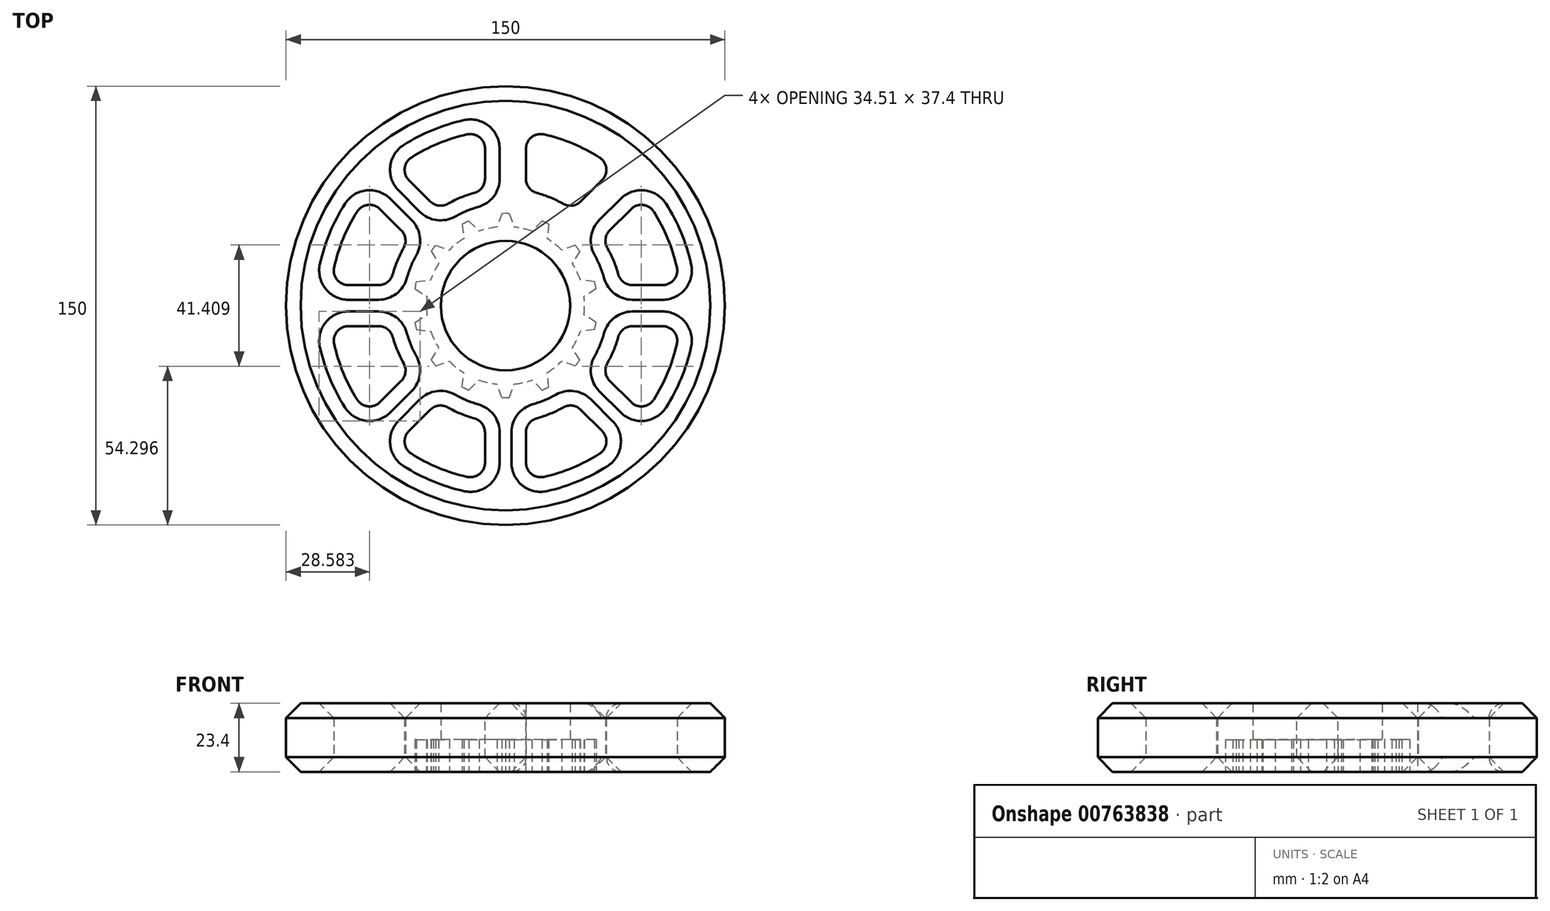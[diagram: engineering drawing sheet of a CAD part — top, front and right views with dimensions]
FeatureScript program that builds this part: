
annotation { "Feature Type Name" : "Feature", "Feature Type Description" : "" }
export const myFeature = defineFeature(function(context is Context, id is Id, definition is map)
    precondition{}
    {
        {
            var Q0;
            Q0=qCreatedBy(makeId("Top.planeOp"),FACE);
            var sketch = newSketch(context, id + "F0", { "sketchPlane" : qUnion([Q0])});
            skCircle(sketch, "E0", {"center": v(0, 0) * mm, "radius": 22.1 * mm});
            skCircle(sketch, "E1", {"center": v(0, 0) * mm, "radius": 75 * mm});
            skSolve(sketch);
        }
        {
            var Q0;
            Q0=qSketchRegion(id+"F0",true);
            extrude(context, id + "F1", {"entities" : qUnion([Q0]), "depth" : 23.4 * mm, "offsetDistance" : 25 * mm});
        }
        {
            var Q0;
            Q0=makeQuery(id+"F1.opExtrude","CAP_FACE",FACE,{"disambiguationData":[OSD([sQuery(id+"F0.wireOp",EDGE,"E0"),sQuery(id+"F0.wireOp",EDGE,"E1")])],"isStart":true});
            var sketch = newSketch(context, id + "F2", { "sketchPlane" : qUnion([Q0])});
            skCircle(sketch, "E2.0", {"center": v(0, 0) * mm, "radius": 22.1 * mm});
            skArc(sketch, "E3", {"start": v(2.9, -26.84) * mm, "mid": v(6, -26.32) * mm, "end": v(9.03, -25.44) * mm});
            skLineSegment(sketch, "E4", {"start": v(0, 0) * mm, "end": v(0, 59.3) * mm, "construction": true});
            skArc(sketch, "E5", {"start": v(0, -31.5) * mm, "mid": v(0.63, -31.5) * mm, "end": v(1.25, -31.48) * mm, "construction": true});
            skLineSegment(sketch, "E6", {"start": v(0, 31.5) * mm, "end": v(-1.25, 31.48) * mm});
            skLineSegment(sketch, "E7.MirrorCS", {"start": v(0, 31.5) * mm, "end": v(1.25, 31.48) * mm});
            skLineSegment(sketch, "E8", {"start": v(-1.25, 31.48) * mm, "end": v(-2.9, 26.84) * mm});
            skLineSegment(sketch, "E9", {"start": v(1.25, 31.48) * mm, "end": v(2.9, 26.84) * mm});
            skArc(sketch, "E10.1.0", {"start": v(0, -31.5) * mm, "mid": v(0.63, -31.5) * mm, "end": v(1.25, -31.48) * mm});
            skLineSegment(sketch, "E11.1.0", {"start": v(-12.53, 28.9) * mm, "end": v(-9.03, 25.44) * mm});
            skLineSegment(sketch, "E11.1.1", {"start": v(-14.78, 27.82) * mm, "end": v(-14.26, 22.93) * mm});
            skLineSegment(sketch, "E11.1.2", {"start": v(-13.67, 28.38) * mm, "end": v(-12.53, 28.9) * mm});
            skLineSegment(sketch, "E11.1.3", {"start": v(-13.67, 28.38) * mm, "end": v(-14.78, 27.82) * mm});
            skLineSegment(sketch, "E11.2.0", {"start": v(-23.83, 20.6) * mm, "end": v(-19.18, 19) * mm});
            skLineSegment(sketch, "E11.2.1", {"start": v(-25.39, 18.65) * mm, "end": v(-22.8, 14.47) * mm});
            skLineSegment(sketch, "E11.2.2", {"start": v(-24.63, 19.64) * mm, "end": v(-23.83, 20.6) * mm});
            skLineSegment(sketch, "E11.2.3", {"start": v(-24.63, 19.64) * mm, "end": v(-25.39, 18.65) * mm});
            skLineSegment(sketch, "E11.3.0", {"start": v(-30.4, 8.22) * mm, "end": v(-25.53, 8.8) * mm});
            skLineSegment(sketch, "E11.3.1", {"start": v(-30.96, 5.79) * mm, "end": v(-26.82, 3.15) * mm});
            skLineSegment(sketch, "E11.3.2", {"start": v(-30.71, 7) * mm, "end": v(-30.4, 8.22) * mm});
            skLineSegment(sketch, "E11.3.3", {"start": v(-30.71, 7) * mm, "end": v(-30.96, 5.79) * mm});
            skLineSegment(sketch, "E11.4.0", {"start": v(-30.96, -5.79) * mm, "end": v(-26.82, -3.15) * mm});
            skLineSegment(sketch, "E11.4.1", {"start": v(-30.4, -8.22) * mm, "end": v(-25.53, -8.8) * mm});
            skLineSegment(sketch, "E11.4.2", {"start": v(-30.71, -7) * mm, "end": v(-30.96, -5.79) * mm});
            skLineSegment(sketch, "E11.4.3", {"start": v(-30.71, -7) * mm, "end": v(-30.4, -8.22) * mm});
            skLineSegment(sketch, "E11.5.0", {"start": v(-25.39, -18.65) * mm, "end": v(-22.8, -14.47) * mm});
            skLineSegment(sketch, "E11.5.1", {"start": v(-23.83, -20.6) * mm, "end": v(-19.18, -19) * mm});
            skLineSegment(sketch, "E11.5.2", {"start": v(-24.63, -19.64) * mm, "end": v(-25.39, -18.65) * mm});
            skLineSegment(sketch, "E11.5.3", {"start": v(-24.63, -19.64) * mm, "end": v(-23.83, -20.6) * mm});
            skLineSegment(sketch, "E11.6.0", {"start": v(-14.78, -27.82) * mm, "end": v(-14.26, -22.93) * mm});
            skLineSegment(sketch, "E11.6.1", {"start": v(-12.53, -28.9) * mm, "end": v(-9.03, -25.44) * mm});
            skLineSegment(sketch, "E11.6.2", {"start": v(-13.67, -28.38) * mm, "end": v(-14.78, -27.82) * mm});
            skLineSegment(sketch, "E11.6.3", {"start": v(-13.67, -28.38) * mm, "end": v(-12.53, -28.9) * mm});
            skLineSegment(sketch, "E11.7.0", {"start": v(-1.25, -31.48) * mm, "end": v(-2.9, -26.84) * mm});
            skLineSegment(sketch, "E11.7.1", {"start": v(1.25, -31.48) * mm, "end": v(2.9, -26.84) * mm});
            skLineSegment(sketch, "E11.7.2", {"start": v(0, -31.5) * mm, "end": v(-1.25, -31.48) * mm});
            skLineSegment(sketch, "E11.7.3", {"start": v(0, -31.5) * mm, "end": v(1.25, -31.48) * mm});
            skLineSegment(sketch, "E11.8.0", {"start": v(12.53, -28.9) * mm, "end": v(9.03, -25.44) * mm});
            skLineSegment(sketch, "E11.8.1", {"start": v(14.78, -27.82) * mm, "end": v(14.26, -22.93) * mm});
            skLineSegment(sketch, "E11.8.2", {"start": v(13.67, -28.38) * mm, "end": v(12.53, -28.9) * mm});
            skLineSegment(sketch, "E11.8.3", {"start": v(13.67, -28.38) * mm, "end": v(14.78, -27.82) * mm});
            skLineSegment(sketch, "E11.9.0", {"start": v(23.83, -20.6) * mm, "end": v(19.18, -19) * mm});
            skLineSegment(sketch, "E11.9.1", {"start": v(25.39, -18.65) * mm, "end": v(22.8, -14.47) * mm});
            skLineSegment(sketch, "E11.9.2", {"start": v(24.63, -19.64) * mm, "end": v(23.83, -20.6) * mm});
            skLineSegment(sketch, "E11.9.3", {"start": v(24.63, -19.64) * mm, "end": v(25.39, -18.65) * mm});
            skLineSegment(sketch, "E11.10.0", {"start": v(30.4, -8.22) * mm, "end": v(25.53, -8.8) * mm});
            skLineSegment(sketch, "E11.10.1", {"start": v(30.96, -5.79) * mm, "end": v(26.82, -3.15) * mm});
            skLineSegment(sketch, "E11.10.2", {"start": v(30.71, -7) * mm, "end": v(30.4, -8.22) * mm});
            skLineSegment(sketch, "E11.10.3", {"start": v(30.71, -7) * mm, "end": v(30.96, -5.79) * mm});
            skLineSegment(sketch, "E11.11.0", {"start": v(30.96, 5.79) * mm, "end": v(26.82, 3.15) * mm});
            skLineSegment(sketch, "E11.11.1", {"start": v(30.4, 8.22) * mm, "end": v(25.53, 8.8) * mm});
            skLineSegment(sketch, "E11.11.2", {"start": v(30.71, 7) * mm, "end": v(30.96, 5.79) * mm});
            skLineSegment(sketch, "E11.11.3", {"start": v(30.71, 7) * mm, "end": v(30.4, 8.22) * mm});
            skLineSegment(sketch, "E11.12.0", {"start": v(25.39, 18.65) * mm, "end": v(22.8, 14.47) * mm});
            skLineSegment(sketch, "E11.12.1", {"start": v(23.83, 20.6) * mm, "end": v(19.18, 19) * mm});
            skLineSegment(sketch, "E11.12.2", {"start": v(24.63, 19.64) * mm, "end": v(25.39, 18.65) * mm});
            skLineSegment(sketch, "E11.12.3", {"start": v(24.63, 19.64) * mm, "end": v(23.83, 20.6) * mm});
            skLineSegment(sketch, "E11.13.0", {"start": v(14.78, 27.82) * mm, "end": v(14.26, 22.93) * mm});
            skLineSegment(sketch, "E11.13.1", {"start": v(12.53, 28.9) * mm, "end": v(9.03, 25.44) * mm});
            skLineSegment(sketch, "E11.13.2", {"start": v(13.67, 28.38) * mm, "end": v(14.78, 27.82) * mm});
            skLineSegment(sketch, "E11.13.3", {"start": v(13.67, 28.38) * mm, "end": v(12.53, 28.9) * mm});
            skArc(sketch, "E12.trimOffspring", {"start": v(-2.9, 26.84) * mm, "mid": v(-6, 26.32) * mm, "end": v(-9.03, 25.44) * mm, "construction": true});
            skPoint(sketch, "E13.start.orphan", {"position": v(0, 27) * mm});
            skArc(sketch, "E14.trimOffspring", {"start": v(-2.9, 26.84) * mm, "mid": v(-6, 26.32) * mm, "end": v(-9.03, 25.44) * mm});
            skArc(sketch, "E15.trimOffspring", {"start": v(-12.53, 28.9) * mm, "mid": v(-13.67, 28.38) * mm, "end": v(-14.78, 27.82) * mm, "construction": true});
            skArc(sketch, "E16.trimOffspring", {"start": v(-12.53, 28.9) * mm, "mid": v(-13.67, 28.38) * mm, "end": v(-14.78, 27.82) * mm});
            skArc(sketch, "E17.trimOffspring", {"start": v(1.25, 31.48) * mm, "mid": v(0, 31.5) * mm, "end": v(-1.25, 31.48) * mm, "construction": true});
            skArc(sketch, "E18.trimOffspring", {"start": v(1.25, 31.48) * mm, "mid": v(0, 31.5) * mm, "end": v(-1.25, 31.48) * mm});
            skArc(sketch, "E19.trimOffspring", {"start": v(9.03, 25.44) * mm, "mid": v(6, 26.32) * mm, "end": v(2.9, 26.84) * mm});
            skArc(sketch, "E20.trimOffspring", {"start": v(14.78, 27.82) * mm, "mid": v(13.67, 28.38) * mm, "end": v(12.53, 28.9) * mm, "construction": true});
            skArc(sketch, "E21.trimOffspring", {"start": v(14.78, 27.82) * mm, "mid": v(13.67, 28.38) * mm, "end": v(12.53, 28.9) * mm});
            skArc(sketch, "E22.trimOffspring", {"start": v(25.39, 18.65) * mm, "mid": v(24.63, 19.64) * mm, "end": v(23.83, 20.6) * mm, "construction": true});
            skArc(sketch, "E23.trimOffspring", {"start": v(19.18, 19) * mm, "mid": v(16.83, 21.1) * mm, "end": v(14.26, 22.93) * mm});
            skArc(sketch, "E24.trimOffspring", {"start": v(25.39, 18.65) * mm, "mid": v(24.63, 19.64) * mm, "end": v(23.83, 20.6) * mm});
            skArc(sketch, "E25.trimOffspring", {"start": v(25.53, 8.8) * mm, "mid": v(24.33, 11.71) * mm, "end": v(22.8, 14.47) * mm});
            skArc(sketch, "E26.trimOffspring", {"start": v(30.96, 5.79) * mm, "mid": v(30.71, 7) * mm, "end": v(30.4, 8.22) * mm, "construction": true});
            skArc(sketch, "E27.trimOffspring", {"start": v(30.96, 5.79) * mm, "mid": v(30.71, 7) * mm, "end": v(30.4, 8.22) * mm});
            skArc(sketch, "E28.trimOffspring", {"start": v(30.4, -8.22) * mm, "mid": v(30.71, -7) * mm, "end": v(30.96, -5.79) * mm, "construction": true});
            skArc(sketch, "E29.trimOffspring", {"start": v(30.4, -8.22) * mm, "mid": v(30.71, -7) * mm, "end": v(30.96, -5.79) * mm});
            skArc(sketch, "E30.trimOffspring", {"start": v(26.82, -3.15) * mm, "mid": v(27, 0) * mm, "end": v(26.82, 3.15) * mm});
            skArc(sketch, "E31.trimOffspring", {"start": v(22.8, -14.47) * mm, "mid": v(24.33, -11.71) * mm, "end": v(25.53, -8.8) * mm});
            skArc(sketch, "E32.trimOffspring", {"start": v(23.83, -20.6) * mm, "mid": v(24.63, -19.64) * mm, "end": v(25.39, -18.65) * mm, "construction": true});
            skArc(sketch, "E33.trimOffspring", {"start": v(23.83, -20.6) * mm, "mid": v(24.63, -19.64) * mm, "end": v(25.39, -18.65) * mm});
            skArc(sketch, "E34.trimOffspring", {"start": v(14.26, -22.93) * mm, "mid": v(16.83, -21.1) * mm, "end": v(19.18, -19) * mm});
            skArc(sketch, "E35.trimOffspring", {"start": v(12.53, -28.9) * mm, "mid": v(13.67, -28.38) * mm, "end": v(14.78, -27.82) * mm, "construction": true});
            skArc(sketch, "E36.trimOffspring", {"start": v(12.53, -28.9) * mm, "mid": v(13.67, -28.38) * mm, "end": v(14.78, -27.82) * mm});
            skPoint(sketch, "E37.orphan", {"position": v(0, -27) * mm});
            skArc(sketch, "E38.trimOffspring", {"start": v(-1.25, -31.48) * mm, "mid": v(-1.07, -31.48) * mm, "end": v(-0.88, -31.49) * mm, "construction": true});
            skArc(sketch, "E39.trimOffspring", {"start": v(-1.25, -31.48) * mm, "mid": v(-1.07, -31.48) * mm, "end": v(-0.88, -31.49) * mm});
            skArc(sketch, "E40.trimOffspring", {"start": v(-9.03, -25.44) * mm, "mid": v(-6, -26.32) * mm, "end": v(-2.9, -26.84) * mm, "construction": true});
            skArc(sketch, "E41.trimOffspring", {"start": v(-9.03, -25.44) * mm, "mid": v(-6, -26.32) * mm, "end": v(-2.9, -26.84) * mm});
            skArc(sketch, "E42.trimOffspring", {"start": v(-14.78, -27.82) * mm, "mid": v(-13.67, -28.38) * mm, "end": v(-12.53, -28.9) * mm, "construction": true});
            skArc(sketch, "E43.trimOffspring", {"start": v(-14.78, -27.82) * mm, "mid": v(-13.67, -28.38) * mm, "end": v(-12.53, -28.9) * mm});
            skArc(sketch, "E44.trimOffspring", {"start": v(-25.39, -18.65) * mm, "mid": v(-24.63, -19.64) * mm, "end": v(-23.83, -20.6) * mm, "construction": true});
            skArc(sketch, "E45.trimOffspring", {"start": v(-25.39, -18.65) * mm, "mid": v(-25.01, -19.15) * mm, "end": v(-24.63, -19.64) * mm});
            skArc(sketch, "E46.trimOffspring", {"start": v(-30.96, -5.79) * mm, "mid": v(-30.84, -6.4) * mm, "end": v(-30.71, -7) * mm, "construction": true});
            skArc(sketch, "E47.trimOffspring", {"start": v(-30.96, -5.79) * mm, "mid": v(-30.84, -6.4) * mm, "end": v(-30.71, -7) * mm});
            skArc(sketch, "E48.trimOffspring", {"start": v(-30.4, 8.22) * mm, "mid": v(-30.71, 7) * mm, "end": v(-30.96, 5.79) * mm, "construction": true});
            skArc(sketch, "E49.trimOffspring", {"start": v(-30.4, 8.22) * mm, "mid": v(-30.71, 7) * mm, "end": v(-30.96, 5.79) * mm});
            skArc(sketch, "E50.trimOffspring", {"start": v(-23.83, 20.6) * mm, "mid": v(-24.63, 19.64) * mm, "end": v(-25.39, 18.65) * mm, "construction": true});
            skArc(sketch, "E51.trimOffspring", {"start": v(-23.83, 20.6) * mm, "mid": v(-24.63, 19.64) * mm, "end": v(-25.39, 18.65) * mm});
            skArc(sketch, "E52.trimOffspring", {"start": v(-19.18, -19) * mm, "mid": v(-16.83, -21.1) * mm, "end": v(-14.26, -22.93) * mm});
            skArc(sketch, "E53.trimOffspring", {"start": v(-25.53, -8.8) * mm, "mid": v(-24.33, -11.71) * mm, "end": v(-22.8, -14.47) * mm});
            skArc(sketch, "E54.trimOffspring", {"start": v(-26.82, 3.15) * mm, "mid": v(-27, 0) * mm, "end": v(-26.82, -3.15) * mm});
            skArc(sketch, "E55.trimOffspring", {"start": v(-22.8, 14.47) * mm, "mid": v(-24.33, 11.71) * mm, "end": v(-25.53, 8.8) * mm, "construction": true});
            skArc(sketch, "E56.trimOffspring", {"start": v(-22.8, 14.47) * mm, "mid": v(-24.33, 11.71) * mm, "end": v(-25.53, 8.8) * mm});
            skArc(sketch, "E57.trimOffspring", {"start": v(-14.26, 22.93) * mm, "mid": v(-16.83, 21.1) * mm, "end": v(-19.18, 19) * mm, "construction": true});
            skArc(sketch, "E58.trimOffspring", {"start": v(-14.26, 22.93) * mm, "mid": v(-16.83, 21.1) * mm, "end": v(-19.18, 19) * mm});
            skSolve(sketch);
        }
        {
            var Q0;
            Q0=qSketchRegion(id+"F2",true);
            extrude(context, id + "F3", {"entities" : qUnion([Q0]), "operationType" : NewBodyOperationType.REMOVE, "oppositeDirection" : true, "depth" : 11 * mm, "offsetDistance" : 25 * mm});
        }
        {
            var Q0;
            Q0=makeQuery(id+"F1.opExtrude","CAP_FACE",FACE,{"disambiguationData":[OSD([sQuery(id+"F0.wireOp",EDGE,"E0"),sQuery(id+"F0.wireOp",EDGE,"E1")])],"isStart":true});
            var sketch = newSketch(context, id + "F4", { "sketchPlane" : qUnion([Q0])});
            skArc(sketch, "E59", {"start": v(-32.8, 22.9) * mm, "mid": v(-36.96, 15.3) * mm, "end": v(-39.38, 7) * mm});
            skArc(sketch, "E60", {"start": v(-47.09, 37.18) * mm, "mid": v(-55.43, 22.96) * mm, "end": v(-59.59, 7) * mm});
            skLineSegment(sketch, "E61", {"start": v(0, 0) * mm, "end": v(0, 117.13) * mm, "construction": true});
            skLineSegment(sketch, "E62", {"start": v(-7, 59.59) * mm, "end": v(-7, 39.38) * mm});
            skLineSegment(sketch, "E63.MirrorCS", {"start": v(7, 59.59) * mm, "end": v(7, 39.38) * mm});
            skLineSegment(sketch, "E64.1.0", {"start": v(-47.09, 37.18) * mm, "end": v(-32.8, 22.9) * mm});
            skLineSegment(sketch, "E64.1.1", {"start": v(-37.18, 47.09) * mm, "end": v(-22.9, 32.8) * mm});
            skLineSegment(sketch, "E64.2.0", {"start": v(-59.59, -7) * mm, "end": v(-39.38, -7) * mm});
            skLineSegment(sketch, "E64.2.1", {"start": v(-59.59, 7) * mm, "end": v(-39.38, 7) * mm});
            skLineSegment(sketch, "E64.3.0", {"start": v(-37.18, -47.09) * mm, "end": v(-22.9, -32.8) * mm});
            skLineSegment(sketch, "E64.3.1", {"start": v(-47.09, -37.18) * mm, "end": v(-32.8, -22.9) * mm});
            skLineSegment(sketch, "E64.4.0", {"start": v(7, -59.59) * mm, "end": v(7, -39.38) * mm});
            skLineSegment(sketch, "E64.4.1", {"start": v(-7, -59.59) * mm, "end": v(-7, -39.38) * mm});
            skLineSegment(sketch, "E64.5.0", {"start": v(47.09, -37.18) * mm, "end": v(32.8, -22.9) * mm});
            skLineSegment(sketch, "E64.5.1", {"start": v(37.18, -47.09) * mm, "end": v(22.9, -32.8) * mm});
            skLineSegment(sketch, "E64.6.0", {"start": v(59.59, 7) * mm, "end": v(39.38, 7) * mm});
            skLineSegment(sketch, "E64.6.1", {"start": v(59.59, -7) * mm, "end": v(39.38, -7) * mm});
            skLineSegment(sketch, "E64.7.0", {"start": v(37.18, 47.09) * mm, "end": v(22.9, 32.8) * mm});
            skLineSegment(sketch, "E64.7.1", {"start": v(47.09, 37.18) * mm, "end": v(32.8, 22.9) * mm});
            skArc(sketch, "E65.trimOffspring", {"start": v(-7, 39.38) * mm, "mid": v(-15.3, 36.96) * mm, "end": v(-22.9, 32.8) * mm});
            skArc(sketch, "E66.trimOffspring", {"start": v(-7, 59.59) * mm, "mid": v(-22.96, 55.43) * mm, "end": v(-37.18, 47.09) * mm});
            skArc(sketch, "E67.trimOffspring", {"start": v(37.18, 47.09) * mm, "mid": v(22.96, 55.43) * mm, "end": v(7, 59.59) * mm});
            skArc(sketch, "E68.trimOffspring", {"start": v(22.9, 32.8) * mm, "mid": v(15.3, 36.96) * mm, "end": v(7, 39.38) * mm});
            skArc(sketch, "E69.trimOffspring", {"start": v(39.38, 7) * mm, "mid": v(36.96, 15.3) * mm, "end": v(32.8, 22.9) * mm});
            skArc(sketch, "E70.trimOffspring", {"start": v(59.59, 7) * mm, "mid": v(55.43, 22.96) * mm, "end": v(47.09, 37.18) * mm});
            skArc(sketch, "E71.trimOffspring", {"start": v(47.09, -37.18) * mm, "mid": v(55.43, -22.96) * mm, "end": v(59.59, -7) * mm});
            skArc(sketch, "E72.trimOffspring", {"start": v(32.8, -22.9) * mm, "mid": v(36.96, -15.3) * mm, "end": v(39.38, -7) * mm});
            skArc(sketch, "E73.trimOffspring", {"start": v(7, -39.38) * mm, "mid": v(15.3, -36.96) * mm, "end": v(22.9, -32.8) * mm});
            skArc(sketch, "E74.trimOffspring", {"start": v(7, -59.59) * mm, "mid": v(22.96, -55.43) * mm, "end": v(37.18, -47.09) * mm});
            skArc(sketch, "E75.trimOffspring", {"start": v(-37.18, -47.09) * mm, "mid": v(-22.96, -55.43) * mm, "end": v(-7, -59.59) * mm});
            skArc(sketch, "E76.trimOffspring", {"start": v(-22.9, -32.8) * mm, "mid": v(-15.3, -36.96) * mm, "end": v(-7, -39.38) * mm});
            skArc(sketch, "E77.trimOffspring", {"start": v(-59.59, -7) * mm, "mid": v(-55.43, -22.96) * mm, "end": v(-47.09, -37.18) * mm});
            skArc(sketch, "E78.trimOffspring", {"start": v(-39.38, -7) * mm, "mid": v(-36.96, -15.3) * mm, "end": v(-32.8, -22.9) * mm});
            skSolve(sketch);
        }
        {
            var Q0;
            Q0=makeQuery(id+"F4.imprint","IMPRINT",FACE,{"disambiguationData":[TD([[makeQuery(id+"F4.imprint","IMPRINT",EDGE,{"derivedFrom":sQuery(id+"F4.wireOp",EDGE,"E59")}),-1.0]])]});
            var Q1;
            Q1=makeQuery(id+"F4.imprint","IMPRINT",FACE,{"disambiguationData":[TD([[makeQuery(id+"F4.imprint","IMPRINT",EDGE,{"derivedFrom":sQuery(id+"F4.wireOp",EDGE,"E62")}),-1.0]])]});
            var Q2;
            Q2=makeQuery(id+"F4.imprint","IMPRINT",FACE,{"disambiguationData":[TD([[makeQuery(id+"F4.imprint","IMPRINT",EDGE,{"derivedFrom":sQuery(id+"F4.wireOp",EDGE,"E63.MirrorCS")}),1.0]])]});
            var Q3;
            Q3=makeQuery(id+"F4.imprint","IMPRINT",FACE,{"disambiguationData":[TD([[makeQuery(id+"F4.imprint","IMPRINT",EDGE,{"derivedFrom":sQuery(id+"F4.wireOp",EDGE,"E64.6.0")}),-1.0]])]});
            var Q4;
            Q4=makeQuery(id+"F4.imprint","IMPRINT",FACE,{"disambiguationData":[TD([[makeQuery(id+"F4.imprint","IMPRINT",EDGE,{"derivedFrom":sQuery(id+"F4.wireOp",EDGE,"E64.5.0")}),-1.0]])]});
            var Q5;
            Q5=makeQuery(id+"F4.imprint","IMPRINT",FACE,{"disambiguationData":[TD([[makeQuery(id+"F4.imprint","IMPRINT",EDGE,{"derivedFrom":sQuery(id+"F4.wireOp",EDGE,"E64.4.0")}),-1.0]])]});
            var Q6;
            Q6=makeQuery(id+"F4.imprint","IMPRINT",FACE,{"disambiguationData":[TD([[makeQuery(id+"F4.imprint","IMPRINT",EDGE,{"derivedFrom":sQuery(id+"F4.wireOp",EDGE,"E64.3.0")}),-1.0]])]});
            var Q7;
            Q7=makeQuery(id+"F4.imprint","IMPRINT",FACE,{"disambiguationData":[TD([[makeQuery(id+"F4.imprint","IMPRINT",EDGE,{"derivedFrom":sQuery(id+"F4.wireOp",EDGE,"E64.2.0")}),-1.0]])]});
            extrude(context, id + "F5", {"entities" : qUnion([Q0, Q1, Q2, Q3, Q4, Q5, Q6, Q7]), "operationType" : NewBodyOperationType.REMOVE, "oppositeDirection" : true, "depth" : 25 * mm, "offsetDistance" : 25 * mm});
        }
        {
            var Q0;
            Q0=makeQuery(id+"F5.boolean.opBoolean","COPY",EDGE,{"derivedFrom":makeQuery(id+"F5.opExtrude","SWEPT_EDGE",EDGE,{"disambiguationData":[OSD([sQuery(id+"F4.wireOp",EDGE,"E60"),sQuery(id+"F4.wireOp",EDGE,"E64.1.0")])]})});
            var Q1;
            Q1=makeQuery(id+"F5.boolean.opBoolean","COPY",EDGE,{"derivedFrom":makeQuery(id+"F5.opExtrude","SWEPT_EDGE",EDGE,{"disambiguationData":[OSD([sQuery(id+"F4.wireOp",EDGE,"E64.1.1"),sQuery(id+"F4.wireOp",EDGE,"E66.trimOffspring")])]})});
            var Q2;
            Q2=makeQuery(id+"F5.boolean.opBoolean","COPY",EDGE,{"derivedFrom":makeQuery(id+"F5.opExtrude","SWEPT_EDGE",EDGE,{"disambiguationData":[OSD([sQuery(id+"F4.wireOp",EDGE,"E59"),sQuery(id+"F4.wireOp",EDGE,"E64.1.0")])]})});
            var Q3;
            Q3=makeQuery(id+"F5.boolean.opBoolean","COPY",EDGE,{"derivedFrom":makeQuery(id+"F5.opExtrude","SWEPT_EDGE",EDGE,{"disambiguationData":[OSD([sQuery(id+"F4.wireOp",EDGE,"E62"),sQuery(id+"F4.wireOp",EDGE,"E65.trimOffspring")])]})});
            var Q4;
            Q4=makeQuery(id+"F5.boolean.opBoolean","COPY",EDGE,{"derivedFrom":makeQuery(id+"F5.opExtrude","SWEPT_EDGE",EDGE,{"disambiguationData":[OSD([sQuery(id+"F4.wireOp",EDGE,"E59"),sQuery(id+"F4.wireOp",EDGE,"E64.2.1")])]})});
            var Q5;
            Q5=makeQuery(id+"F5.boolean.opBoolean","COPY",EDGE,{"derivedFrom":makeQuery(id+"F5.opExtrude","SWEPT_EDGE",EDGE,{"disambiguationData":[OSD([sQuery(id+"F4.wireOp",EDGE,"E64.7.0"),sQuery(id+"F4.wireOp",EDGE,"E68.trimOffspring")])]})});
            var Q6;
            Q6=makeQuery(id+"F5.boolean.opBoolean","COPY",EDGE,{"derivedFrom":makeQuery(id+"F5.opExtrude","SWEPT_EDGE",EDGE,{"disambiguationData":[OSD([sQuery(id+"F4.wireOp",EDGE,"E64.5.1"),sQuery(id+"F4.wireOp",EDGE,"E74.trimOffspring")])]})});
            var Q7;
            Q7=makeQuery(id+"F5.boolean.opBoolean","COPY",EDGE,{"derivedFrom":makeQuery(id+"F5.opExtrude","SWEPT_EDGE",EDGE,{"disambiguationData":[OSD([sQuery(id+"F4.wireOp",EDGE,"E64.3.1"),sQuery(id+"F4.wireOp",EDGE,"E78.trimOffspring")])]})});
            var Q8;
            Q8=makeQuery(id+"F5.boolean.opBoolean","COPY",EDGE,{"derivedFrom":makeQuery(id+"F5.opExtrude","SWEPT_EDGE",EDGE,{"disambiguationData":[OSD([sQuery(id+"F4.wireOp",EDGE,"E64.4.1"),sQuery(id+"F4.wireOp",EDGE,"E76.trimOffspring")])]})});
            var Q9;
            Q9=makeQuery(id+"F5.boolean.opBoolean","COPY",EDGE,{"derivedFrom":makeQuery(id+"F5.opExtrude","SWEPT_EDGE",EDGE,{"disambiguationData":[OSD([sQuery(id+"F4.wireOp",EDGE,"E64.2.0"),sQuery(id+"F4.wireOp",EDGE,"E78.trimOffspring")])]})});
            var Q10;
            Q10=makeQuery(id+"F5.boolean.opBoolean","COPY",EDGE,{"derivedFrom":makeQuery(id+"F5.opExtrude","SWEPT_EDGE",EDGE,{"disambiguationData":[OSD([sQuery(id+"F4.wireOp",EDGE,"E64.3.0"),sQuery(id+"F4.wireOp",EDGE,"E76.trimOffspring")])]})});
            var Q11;
            Q11=makeQuery(id+"F5.boolean.opBoolean","COPY",EDGE,{"derivedFrom":makeQuery(id+"F5.opExtrude","SWEPT_EDGE",EDGE,{"disambiguationData":[OSD([sQuery(id+"F4.wireOp",EDGE,"E64.4.0"),sQuery(id+"F4.wireOp",EDGE,"E73.trimOffspring")])]})});
            var Q12;
            Q12=makeQuery(id+"F5.boolean.opBoolean","COPY",EDGE,{"derivedFrom":makeQuery(id+"F5.opExtrude","SWEPT_EDGE",EDGE,{"disambiguationData":[OSD([sQuery(id+"F4.wireOp",EDGE,"E64.5.1"),sQuery(id+"F4.wireOp",EDGE,"E73.trimOffspring")])]})});
            var Q13;
            Q13=makeQuery(id+"F5.boolean.opBoolean","COPY",EDGE,{"derivedFrom":makeQuery(id+"F5.opExtrude","SWEPT_EDGE",EDGE,{"disambiguationData":[OSD([sQuery(id+"F4.wireOp",EDGE,"E64.5.0"),sQuery(id+"F4.wireOp",EDGE,"E72.trimOffspring")])]})});
            var Q14;
            Q14=makeQuery(id+"F5.boolean.opBoolean","COPY",EDGE,{"derivedFrom":makeQuery(id+"F5.opExtrude","SWEPT_EDGE",EDGE,{"disambiguationData":[OSD([sQuery(id+"F4.wireOp",EDGE,"E64.6.1"),sQuery(id+"F4.wireOp",EDGE,"E72.trimOffspring")])]})});
            var Q15;
            Q15=makeQuery(id+"F5.boolean.opBoolean","COPY",EDGE,{"derivedFrom":makeQuery(id+"F5.opExtrude","SWEPT_EDGE",EDGE,{"disambiguationData":[OSD([sQuery(id+"F4.wireOp",EDGE,"E64.6.0"),sQuery(id+"F4.wireOp",EDGE,"E69.trimOffspring")])]})});
            var Q16;
            Q16=makeQuery(id+"F5.boolean.opBoolean","COPY",EDGE,{"derivedFrom":makeQuery(id+"F5.opExtrude","SWEPT_EDGE",EDGE,{"disambiguationData":[OSD([sQuery(id+"F4.wireOp",EDGE,"E64.7.1"),sQuery(id+"F4.wireOp",EDGE,"E69.trimOffspring")])]})});
            var Q17;
            Q17=makeQuery(id+"F5.boolean.opBoolean","COPY",EDGE,{"derivedFrom":makeQuery(id+"F5.opExtrude","SWEPT_EDGE",EDGE,{"disambiguationData":[OSD([sQuery(id+"F4.wireOp",EDGE,"E63.MirrorCS"),sQuery(id+"F4.wireOp",EDGE,"E68.trimOffspring")])]})});
            var Q18;
            Q18=makeQuery(id+"F5.boolean.opBoolean","COPY",EDGE,{"derivedFrom":makeQuery(id+"F5.opExtrude","SWEPT_EDGE",EDGE,{"disambiguationData":[OSD([sQuery(id+"F4.wireOp",EDGE,"E64.1.1"),sQuery(id+"F4.wireOp",EDGE,"E65.trimOffspring")])]})});
            var Q19;
            Q19=makeQuery(id+"F5.boolean.opBoolean","COPY",EDGE,{"derivedFrom":makeQuery(id+"F5.opExtrude","SWEPT_EDGE",EDGE,{"disambiguationData":[OSD([sQuery(id+"F4.wireOp",EDGE,"E64.5.0"),sQuery(id+"F4.wireOp",EDGE,"E71.trimOffspring")])]})});
            var Q20;
            Q20=makeQuery(id+"F5.boolean.opBoolean","COPY",FACE,{"derivedFrom":makeQuery(id+"F5.opExtrude","SWEPT_FACE",FACE,{"disambiguationData":[OSD([sQuery(id+"F4.wireOp",EDGE,"E74.trimOffspring")])]})});
            var Q21;
            Q21=makeQuery(id+"F5.boolean.opBoolean","COPY",EDGE,{"derivedFrom":makeQuery(id+"F5.opExtrude","SWEPT_EDGE",EDGE,{"disambiguationData":[OSD([sQuery(id+"F4.wireOp",EDGE,"E64.4.1"),sQuery(id+"F4.wireOp",EDGE,"E75.trimOffspring")])]})});
            var Q22;
            Q22=makeQuery(id+"F5.boolean.opBoolean","COPY",EDGE,{"derivedFrom":makeQuery(id+"F5.opExtrude","SWEPT_EDGE",EDGE,{"disambiguationData":[OSD([sQuery(id+"F4.wireOp",EDGE,"E64.3.0"),sQuery(id+"F4.wireOp",EDGE,"E75.trimOffspring")])]})});
            var Q23;
            Q23=makeQuery(id+"F5.boolean.opBoolean","COPY",EDGE,{"derivedFrom":makeQuery(id+"F5.opExtrude","SWEPT_EDGE",EDGE,{"disambiguationData":[OSD([sQuery(id+"F4.wireOp",EDGE,"E64.3.1"),sQuery(id+"F4.wireOp",EDGE,"E77.trimOffspring")])]})});
            var Q24;
            Q24=makeQuery(id+"F5.boolean.opBoolean","COPY",EDGE,{"derivedFrom":makeQuery(id+"F5.opExtrude","SWEPT_EDGE",EDGE,{"disambiguationData":[OSD([sQuery(id+"F4.wireOp",EDGE,"E64.2.0"),sQuery(id+"F4.wireOp",EDGE,"E77.trimOffspring")])]})});
            var Q25;
            Q25=makeQuery(id+"F5.boolean.opBoolean","COPY",EDGE,{"derivedFrom":makeQuery(id+"F5.opExtrude","SWEPT_EDGE",EDGE,{"disambiguationData":[OSD([sQuery(id+"F4.wireOp",EDGE,"E60"),sQuery(id+"F4.wireOp",EDGE,"E64.2.1")])]})});
            var Q26;
            Q26=makeQuery(id+"F5.boolean.opBoolean","COPY",EDGE,{"derivedFrom":makeQuery(id+"F5.opExtrude","SWEPT_EDGE",EDGE,{"disambiguationData":[OSD([sQuery(id+"F4.wireOp",EDGE,"E62"),sQuery(id+"F4.wireOp",EDGE,"E66.trimOffspring")])]})});
            var Q27;
            Q27=makeQuery(id+"F5.boolean.opBoolean","COPY",EDGE,{"derivedFrom":makeQuery(id+"F5.opExtrude","SWEPT_EDGE",EDGE,{"disambiguationData":[OSD([sQuery(id+"F4.wireOp",EDGE,"E63.MirrorCS"),sQuery(id+"F4.wireOp",EDGE,"E67.trimOffspring")])]})});
            var Q28;
            Q28=makeQuery(id+"F5.boolean.opBoolean","COPY",EDGE,{"derivedFrom":makeQuery(id+"F5.opExtrude","SWEPT_EDGE",EDGE,{"disambiguationData":[OSD([sQuery(id+"F4.wireOp",EDGE,"E64.7.0"),sQuery(id+"F4.wireOp",EDGE,"E67.trimOffspring")])]})});
            var Q29;
            Q29=makeQuery(id+"F5.boolean.opBoolean","COPY",EDGE,{"derivedFrom":makeQuery(id+"F5.opExtrude","SWEPT_EDGE",EDGE,{"disambiguationData":[OSD([sQuery(id+"F4.wireOp",EDGE,"E64.7.1"),sQuery(id+"F4.wireOp",EDGE,"E70.trimOffspring")])]})});
            var Q30;
            Q30=makeQuery(id+"F5.boolean.opBoolean","COPY",EDGE,{"derivedFrom":makeQuery(id+"F5.opExtrude","SWEPT_EDGE",EDGE,{"disambiguationData":[OSD([sQuery(id+"F4.wireOp",EDGE,"E64.6.0"),sQuery(id+"F4.wireOp",EDGE,"E70.trimOffspring")])]})});
            var Q31;
            Q31=makeQuery(id+"F5.boolean.opBoolean","COPY",EDGE,{"derivedFrom":makeQuery(id+"F5.opExtrude","SWEPT_EDGE",EDGE,{"disambiguationData":[OSD([sQuery(id+"F4.wireOp",EDGE,"E64.6.1"),sQuery(id+"F4.wireOp",EDGE,"E71.trimOffspring")])]})});
            fillet(context, id + "F6", {"entities" : qUnion([Q0, Q1, Q2, Q3, Q4, Q5, Q6, Q7, Q8, Q9, Q10, Q11, Q12, Q13, Q14, Q15, Q16, Q17, Q18, Q19, Q20, Q21, Q22, Q23, Q24, Q25, Q26, Q27, Q28, Q29, Q30, Q31]), "radius" : 5 * mm, "tangentPropagation" : true, "allowEdgeOverflow" : false});
        }
        {
            var Q0;
            Q0=makeQuery(id+"F1.opExtrude","CAP_EDGE",EDGE,{"disambiguationData":[OSD([sQuery(id+"F0.wireOp",EDGE,"E1")])],"isStart":false});
            var Q1;
            Q1=makeQuery(id+"F1.opExtrude","CAP_EDGE",EDGE,{"disambiguationData":[OSD([sQuery(id+"F0.wireOp",EDGE,"E1")])],"isStart":true});
            var Q2;
            Q2=makeQuery(id+"F5.boolean.opBoolean","COPY",EDGE,{"derivedFrom":makeQuery(id+"F5.opExtrude","CAP_EDGE",EDGE,{"disambiguationData":[OSD([sQuery(id+"F4.wireOp",EDGE,"E75.trimOffspring")])],"isStart":true})});
            var Q3;
            Q3=makeQuery(id+"F5.boolean.opBoolean","COPY",FACE,{"derivedFrom":makeQuery(id+"F5.opExtrude","SWEPT_FACE",FACE,{"disambiguationData":[OSD([sQuery(id+"F4.wireOp",EDGE,"E77.trimOffspring")])]})});
            var Q4;
            Q4=makeQuery(id+"F5.boolean.opBoolean","COPY",FACE,{"derivedFrom":makeQuery(id+"F5.opExtrude","SWEPT_FACE",FACE,{"disambiguationData":[OSD([sQuery(id+"F4.wireOp",EDGE,"E75.trimOffspring")])]})});
            var Q5;
            Q5=makeQuery(id+"F5.boolean.opBoolean","COPY",FACE,{"derivedFrom":makeQuery(id+"F5.opExtrude","SWEPT_FACE",FACE,{"disambiguationData":[OSD([sQuery(id+"F4.wireOp",EDGE,"E60")])]})});
            var Q6;
            Q6=makeQuery(id+"F5.boolean.opBoolean","COPY",FACE,{"derivedFrom":makeQuery(id+"F5.opExtrude","SWEPT_FACE",FACE,{"disambiguationData":[OSD([sQuery(id+"F4.wireOp",EDGE,"E66.trimOffspring")])]})});
            var Q7;
            Q7=makeQuery(id+"F5.boolean.opBoolean","COPY",FACE,{"derivedFrom":makeQuery(id+"F5.opExtrude","SWEPT_FACE",FACE,{"disambiguationData":[OSD([sQuery(id+"F4.wireOp",EDGE,"E67.trimOffspring")])]})});
            var Q8;
            Q8=makeQuery(id+"F5.boolean.opBoolean","COPY",FACE,{"derivedFrom":makeQuery(id+"F5.opExtrude","SWEPT_FACE",FACE,{"disambiguationData":[OSD([sQuery(id+"F4.wireOp",EDGE,"E64.7.1")])]})});
            var Q9;
            Q9=makeQuery(id+"F5.boolean.opBoolean","INTERSECT",EDGE,{"derivedFrom":[makeQuery(id+"F1.opExtrude","CAP_FACE",FACE,{"disambiguationData":[OSD([sQuery(id+"F0.wireOp",EDGE,"E0"),sQuery(id+"F0.wireOp",EDGE,"E1")])],"isStart":false}),makeQuery(id+"F5.opExtrude","SWEPT_FACE",FACE,{"disambiguationData":[OSD([sQuery(id+"F4.wireOp",EDGE,"E64.5.0")])]})]});
            var Q10;
            Q10=makeQuery(id+"F5.boolean.opBoolean","COPY",FACE,{"derivedFrom":makeQuery(id+"F5.opExtrude","SWEPT_FACE",FACE,{"disambiguationData":[OSD([sQuery(id+"F4.wireOp",EDGE,"E64.5.0")])]})});
            chamfer(context, id + "F7", {"entities" : qUnion([Q0, Q1, Q2, Q3, Q4, Q5, Q6, Q7, Q8, Q9, Q10]), "width" : 5 * mm, "tangentPropagation" : true});
        }
    });
